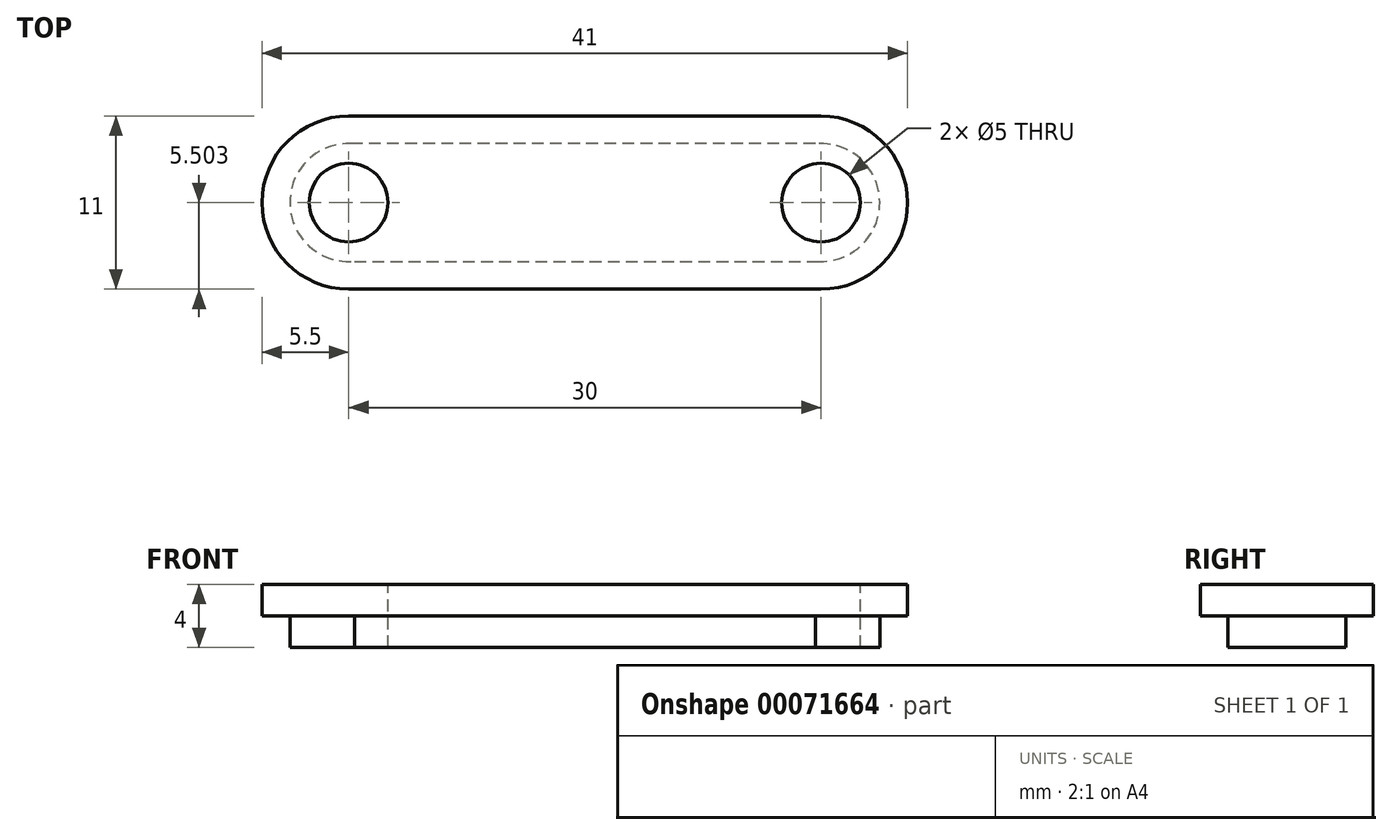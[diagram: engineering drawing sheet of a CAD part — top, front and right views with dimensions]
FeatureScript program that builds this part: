
annotation { "Feature Type Name" : "Feature", "Feature Type Description" : "" }
export const myFeature = defineFeature(function(context is Context, id is Id, definition is map)
    precondition{}
    {
        {
            var Q0;
            Q0=qCreatedBy(makeId("Top.planeOp"),FACE);
            var sketch = newSketch(context, id + "F0", { "sketchPlane" : qUnion([Q0])});
            skLineSegment(sketch, "E0.7", {"start": v(15, 5.5) * mm, "end": v(-15, 5.5) * mm});
            skLineSegment(sketch, "E0.6", {"start": v(15, 4) * mm, "end": v(-15, 4) * mm, "construction": true});
            skArc(sketch, "E0.11", {"start": v(19, 0.04) * mm, "mid": v(17.85, -2.82) * mm, "end": v(15, -4) * mm, "construction": true});
            skArc(sketch, "E0.8", {"start": v(15, 4) * mm, "mid": v(17.81, 2.84) * mm, "end": v(19, 0.04) * mm, "construction": true});
            skArc(sketch, "E0.10", {"start": v(15, -5.5) * mm, "mid": v(18.91, -3.88) * mm, "end": v(20.5, 0.05) * mm});
            skArc(sketch, "E0.9", {"start": v(20.5, 0.05) * mm, "mid": v(18.87, 3.9) * mm, "end": v(15, 5.5) * mm});
            skArc(sketch, "E0.0", {"start": v(-15, 5.5) * mm, "mid": v(-18.89, 3.88) * mm, "end": v(-20.5, 0) * mm});
            skArc(sketch, "E0.1", {"start": v(-20.5, 0) * mm, "mid": v(-18.89, -3.9) * mm, "end": v(-15, -5.5) * mm});
            skLineSegment(sketch, "E0.2", {"start": v(-15, -5.5) * mm, "end": v(15, -5.5) * mm});
            skLineSegment(sketch, "E0.3", {"start": v(-15, -4) * mm, "end": v(15, -4) * mm, "construction": true});
            skArc(sketch, "E0.4", {"start": v(-15, -4) * mm, "mid": v(-17.83, -2.84) * mm, "end": v(-19, 0) * mm, "construction": true});
            skArc(sketch, "E0.5", {"start": v(-19, 0) * mm, "mid": v(-17.83, 2.82) * mm, "end": v(-15, 4) * mm, "construction": true});
            skSolve(sketch);
        }
        {
            var Q0;
            Q0=makeQuery(id+"F0.imprint","IMPRINT",FACE,{"disambiguationData":[TD([[makeQuery(id+"F0.imprint","IMPRINT",EDGE,{"derivedFrom":sQuery(id+"F0.wireOp",EDGE,"E0.7")}),1.0]])]});
            var Q1;
            Q1=sQuery(id+"F0.wireOp",EDGE,"795070f1-f786-4fbf-82b9-3b82b4b4287f.7");
            var Q2;
            Q2=sQuery(id+"F0.wireOp",EDGE,"795070f1-f786-4fbf-82b9-3b82b4b4287f.0");
            var Q3;
            Q3=sQuery(id+"F0.wireOp",EDGE,"795070f1-f786-4fbf-82b9-3b82b4b4287f.1");
            var Q4;
            Q4=sQuery(id+"F0.wireOp",EDGE,"795070f1-f786-4fbf-82b9-3b82b4b4287f.2");
            var Q5;
            Q5=sQuery(id+"F0.wireOp",EDGE,"795070f1-f786-4fbf-82b9-3b82b4b4287f.10");
            var Q6;
            Q6=sQuery(id+"F0.wireOp",EDGE,"795070f1-f786-4fbf-82b9-3b82b4b4287f.9");
            extrude(context, id + "F1", {"entities" : qUnion([Q0]), "surfaceEntities" : qUnion([Q1, Q2, Q3, Q4, Q5, Q6]), "depth" : 2 * mm});
        }
        {
            var Q0;
            Q0=makeQuery(id+"F1.opExtrude","CAP_FACE",FACE,{"disambiguationData":[OSD([sQuery(id+"F0.wireOp",EDGE,"E0.7"),sQuery(id+"F0.wireOp",EDGE,"E0.10"),sQuery(id+"F0.wireOp",EDGE,"E0.9"),sQuery(id+"F0.wireOp",EDGE,"E0.0"),sQuery(id+"F0.wireOp",EDGE,"E0.1"),sQuery(id+"F0.wireOp",EDGE,"E0.2")])],"isStart":true});
            var sketch = newSketch(context, id + "F2", { "sketchPlane" : qUnion([Q0])});
            skArc(sketch, "E1.0", {"start": v(-15, -5.5) * mm, "mid": v(-20.5, 0) * mm, "end": v(-15, 5.5) * mm, "construction": true});
            skLineSegment(sketch, "E1.1", {"start": v(-15, 5.5) * mm, "end": v(15, 5.5) * mm, "construction": true});
            skArc(sketch, "E1.2", {"start": v(15, 5.5) * mm, "mid": v(20.5, 0) * mm, "end": v(15, -5.5) * mm, "construction": true});
            skLineSegment(sketch, "E1.3", {"start": v(15, -5.5) * mm, "end": v(-15, -5.5) * mm, "construction": true});
            skLineSegment(sketch, "E2.0", {"start": v(-14.64, 3.73) * mm, "end": v(14.64, 3.73) * mm});
            skArc(sketch, "E2.1", {"start": v(-14.64, -3.73) * mm, "mid": v(-18.73, 0) * mm, "end": v(-14.64, 3.73) * mm});
            skLineSegment(sketch, "E2.2", {"start": v(14.64, -3.73) * mm, "end": v(-14.64, -3.73) * mm});
            skArc(sketch, "E2.3", {"start": v(14.64, 3.73) * mm, "mid": v(18.73, 0) * mm, "end": v(14.64, -3.73) * mm});
            skPoint(sketch, "E3", {"position": v(-18.73, 0) * mm});
            skPoint(sketch, "E4", {"position": v(-20.5, 0) * mm});
            skPoint(sketch, "E5", {"position": v(20.5, 0) * mm});
            skPoint(sketch, "E6", {"position": v(18.73, 0) * mm});
            skPoint(sketch, "E7", {"position": v(0, 5.5) * mm});
            skPoint(sketch, "E8", {"position": v(0, 3.73) * mm});
            skPoint(sketch, "E9", {"position": v(0, -3.73) * mm});
            skPoint(sketch, "E10", {"position": v(0, -5.5) * mm});
            skSolve(sketch);
        }
        {
            var Q0;
            Q0=makeQuery(id+"F2.imprint","IMPRINT",FACE,{"disambiguationData":[TD([[makeQuery(id+"F2.imprint","IMPRINT",EDGE,{"derivedFrom":sQuery(id+"F2.wireOp",EDGE,"E2.0")}),-1.0]])]});
            extrude(context, id + "F3", {"entities" : qUnion([Q0]), "operationType" : NewBodyOperationType.ADD, "depth" : 2 * mm});
        }
        {
            var Q0;
            Q0=makeQuery(id+"F1.opExtrude","CAP_FACE",FACE,{"disambiguationData":[OSD([sQuery(id+"F0.wireOp",EDGE,"E0.7"),sQuery(id+"F0.wireOp",EDGE,"E0.10"),sQuery(id+"F0.wireOp",EDGE,"E0.9"),sQuery(id+"F0.wireOp",EDGE,"E0.0"),sQuery(id+"F0.wireOp",EDGE,"E0.1"),sQuery(id+"F0.wireOp",EDGE,"E0.2")])],"isStart":false});
            var sketch = newSketch(context, id + "F4", { "sketchPlane" : qUnion([Q0])});
            skCircle(sketch, "E11", {"center": v(-15, 0) * mm, "radius": 2.5 * mm});
            skCircle(sketch, "E12", {"center": v(15, 0) * mm, "radius": 2.5 * mm});
            skArc(sketch, "E13.0", {"start": v(-15, 5.5) * mm, "mid": v(-20.5, 0) * mm, "end": v(-15, -5.5) * mm, "construction": true});
            skArc(sketch, "E13.1", {"start": v(15, -5.5) * mm, "mid": v(20.5, 0) * mm, "end": v(15, 5.5) * mm, "construction": true});
            skSolve(sketch);
        }
        {
            var Q0;
            Q0 = qSketchRegion(id + "F4", true);
            extrude(context, id + "F5", {"entities" : qUnion([Q0]), "operationType" : NewBodyOperationType.REMOVE, "endBound" : BoundingType.THROUGH_ALL, "oppositeDirection" : true, "depth" : 25 * mm});
        }
    });
